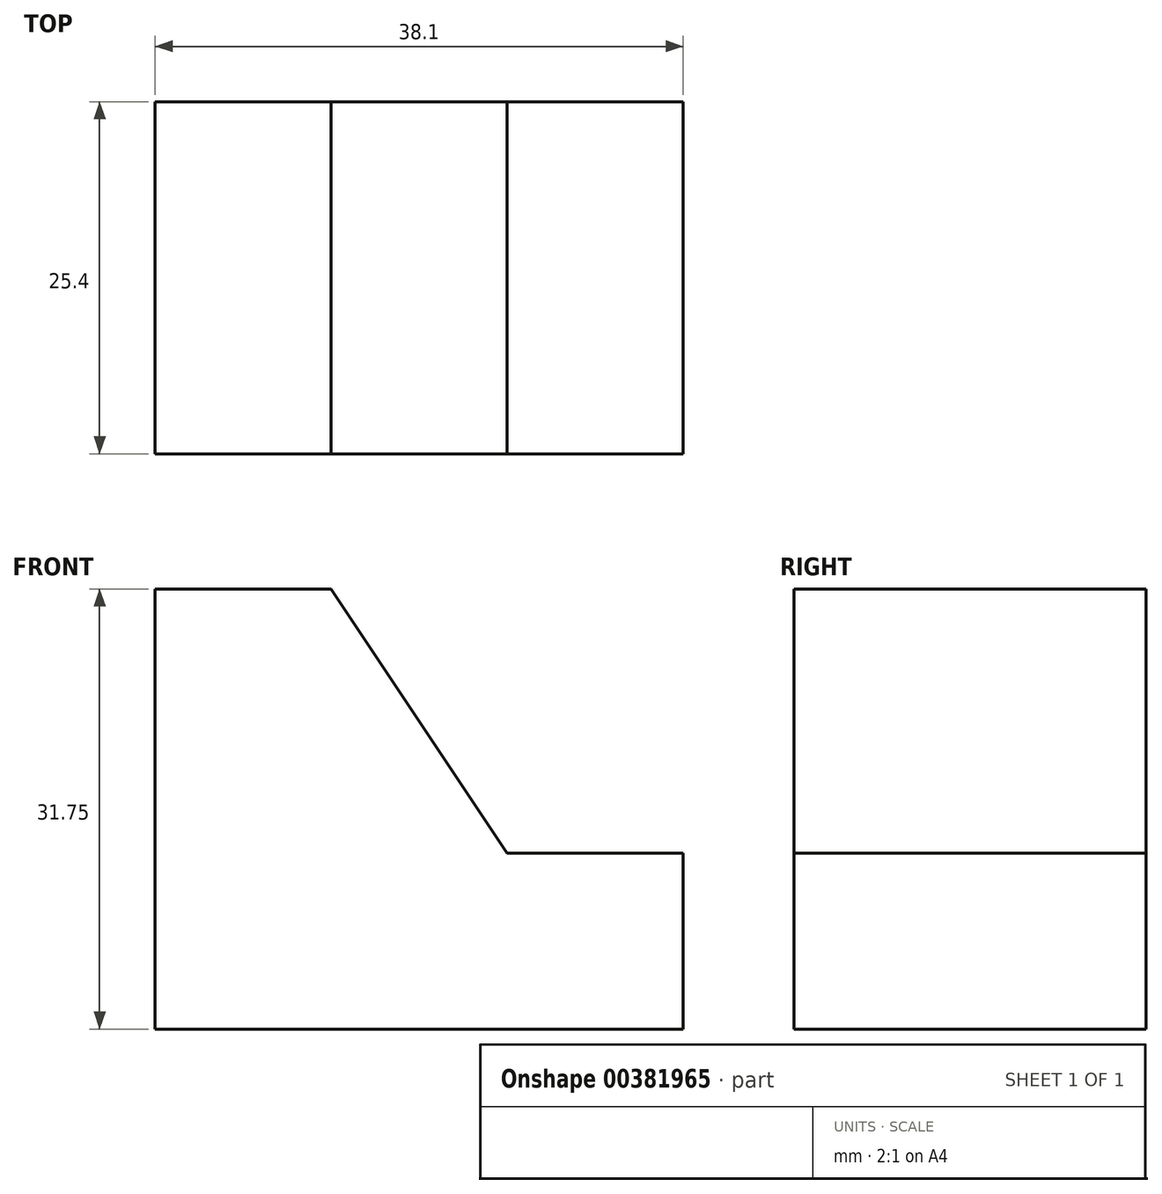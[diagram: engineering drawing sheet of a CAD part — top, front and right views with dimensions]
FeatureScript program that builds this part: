
annotation { "Feature Type Name" : "Feature", "Feature Type Description" : "" }
export const myFeature = defineFeature(function(context is Context, id is Id, definition is map)
    precondition{}
    {
        {
            var Q0;
            Q0=qCreatedBy(makeId("Front.planeOp"),FACE);
            var sketch = newSketch(context, id + "F0", { "sketchPlane" : qUnion([Q0])});
            skLineSegment(sketch, "E0", {"start": v(-52.92, 31.75) * mm, "end": v(-52.92, 0) * mm});
            skLineSegment(sketch, "E1", {"start": v(-52.92, 0) * mm, "end": v(-14.82, 0) * mm});
            skLineSegment(sketch, "E2", {"start": v(-14.82, 0) * mm, "end": v(-14.82, 12.7) * mm});
            skLineSegment(sketch, "E3", {"start": v(-14.82, 12.7) * mm, "end": v(-27.52, 12.7) * mm});
            skLineSegment(sketch, "E4", {"start": v(-27.52, 12.7) * mm, "end": v(-40.22, 31.75) * mm});
            skLineSegment(sketch, "E5", {"start": v(-40.22, 31.75) * mm, "end": v(-52.92, 31.75) * mm});
            skSolve(sketch);
        }
        {
            var Q0;
            Q0=makeQuery(id+"F0.imprint","IMPRINT",FACE,{"disambiguationData":[TD([[makeQuery(id+"F0.imprint","IMPRINT",EDGE,{"derivedFrom":sQuery(id+"F0.wireOp",EDGE,"E0")}),1.0]])]});
            extrude(context, id + "F1", {"entities" : qUnion([Q0]), "depth" : 25.4 * mm, "offsetDistance" : 25.4 * mm});
        }
    });
